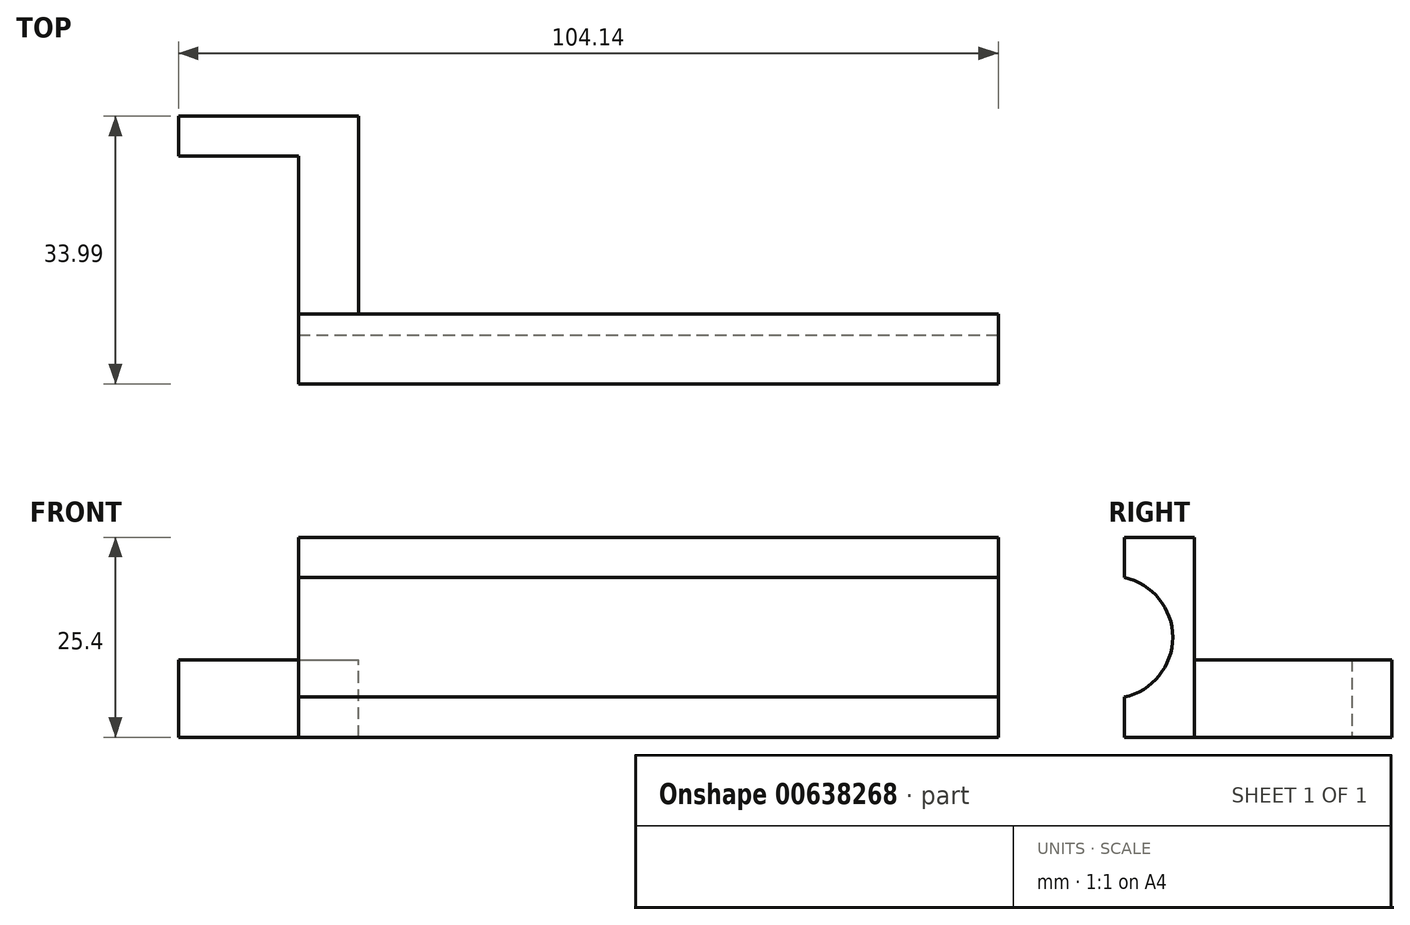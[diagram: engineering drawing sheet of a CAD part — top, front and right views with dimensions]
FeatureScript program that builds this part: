
annotation { "Feature Type Name" : "Feature", "Feature Type Description" : "" }
export const myFeature = defineFeature(function(context is Context, id is Id, definition is map)
    precondition{}
    {
        {
            var Q0;
            Q0=qCreatedBy(makeId("Front.planeOp"),FACE);
            var sketch = newSketch(context, id + "F0", { "sketchPlane" : qUnion([Q0])});
            skLineSegment(sketch, "E0.bottom", {"start": v(0, 0) * mm, "end": v(-88.9, 0) * mm});
            skLineSegment(sketch, "E0.top", {"start": v(0, 25.4) * mm, "end": v(-88.9, 25.4) * mm});
            skLineSegment(sketch, "E0.left", {"start": v(0, 0) * mm, "end": v(0, 25.4) * mm});
            skLineSegment(sketch, "E0.right", {"start": v(-88.9, 0) * mm, "end": v(-88.9, 25.4) * mm});
            skSolve(sketch);
        }
        {
            var Q0;
            Q0=qSketchRegion(id+"F0",true);
            extrude(context, id + "F1", {"entities" : qUnion([Q0]), "depth" : 8.9 * mm, "offsetDistance" : 25.4 * mm});
        }
        {
            var Q0;
            Q0=makeQuery(id+"F1.opExtrude","SWEPT_FACE",FACE,{"disambiguationData":[OSD([sQuery(id+"F0.wireOp",EDGE,"E0.right")])]});
            var sketch = newSketch(context, id + "F2", { "sketchPlane" : qUnion([Q0])});
            skCircle(sketch, "E1", {"center": v(10.48, 12.7) * mm, "radius": 7.75 * mm});
            skSolve(sketch);
        }
        {
            var Q0;
            Q0=qSketchRegion(id+"F2",true);
            extrude(context, id + "F3", {"entities" : qUnion([Q0]), "operationType" : NewBodyOperationType.REMOVE, "endBound" : BoundingType.THROUGH_ALL, "oppositeDirection" : true, "depth" : 25.4 * mm, "offsetDistance" : 25.4 * mm});
        }
        {
            var Q0;
            Q0=makeQuery(id+"F1.opExtrude","CAP_FACE",FACE,{"disambiguationData":[OSD([sQuery(id+"F0.wireOp",EDGE,"E0.bottom"),sQuery(id+"F0.wireOp",EDGE,"E0.top"),sQuery(id+"F0.wireOp",EDGE,"E0.left"),sQuery(id+"F0.wireOp",EDGE,"E0.right")])],"isStart":true});
            var sketch = newSketch(context, id + "F4", { "sketchPlane" : qUnion([Q0])});
            skLineSegment(sketch, "E2.bottom", {"start": v(88.9, 0) * mm, "end": v(81.28, 0) * mm});
            skLineSegment(sketch, "E2.top", {"start": v(88.9, 9.86) * mm, "end": v(81.28, 9.86) * mm});
            skLineSegment(sketch, "E2.left", {"start": v(88.9, 0) * mm, "end": v(88.9, 9.86) * mm});
            skLineSegment(sketch, "E2.right", {"start": v(81.28, 0) * mm, "end": v(81.28, 9.86) * mm});
            skSolve(sketch);
        }
        {
            var Q0;
            Q0=qSketchRegion(id+"F4",true);
            extrude(context, id + "F5", {"entities" : qUnion([Q0]), "operationType" : NewBodyOperationType.ADD, "depth" : 25.1 * mm, "offsetDistance" : 25.4 * mm});
        }
        {
            var Q0;
            Q0=makeQuery(id+"F5.boolean.opBoolean","MERGE",FACE,{"derivedFrom":[makeQuery(id+"F1.opExtrude","SWEPT_FACE",FACE,{"disambiguationData":[OSD([sQuery(id+"F0.wireOp",EDGE,"E0.right")])]}),makeQuery(id+"F5.opExtrude","SWEPT_FACE",FACE,{"disambiguationData":[OSD([sQuery(id+"F4.wireOp",EDGE,"E2.left")])]})]});
            var sketch = newSketch(context, id + "F6", { "sketchPlane" : qUnion([Q0])});
            skLineSegment(sketch, "E3.bottom", {"start": v(-25.1, 9.86) * mm, "end": v(-20.02, 9.86) * mm});
            skLineSegment(sketch, "E3.top", {"start": v(-25.1, 0) * mm, "end": v(-20.02, 0) * mm});
            skLineSegment(sketch, "E3.left", {"start": v(-25.1, 9.86) * mm, "end": v(-25.1, 0) * mm});
            skLineSegment(sketch, "E3.right", {"start": v(-20.02, 9.86) * mm, "end": v(-20.02, 0) * mm});
            skSolve(sketch);
        }
        {
            var Q0;
            Q0=qSketchRegion(id+"F6",true);
            extrude(context, id + "F7", {"entities" : qUnion([Q0]), "operationType" : NewBodyOperationType.ADD, "depth" : 15.24 * mm, "offsetDistance" : 25.4 * mm});
        }
    });
